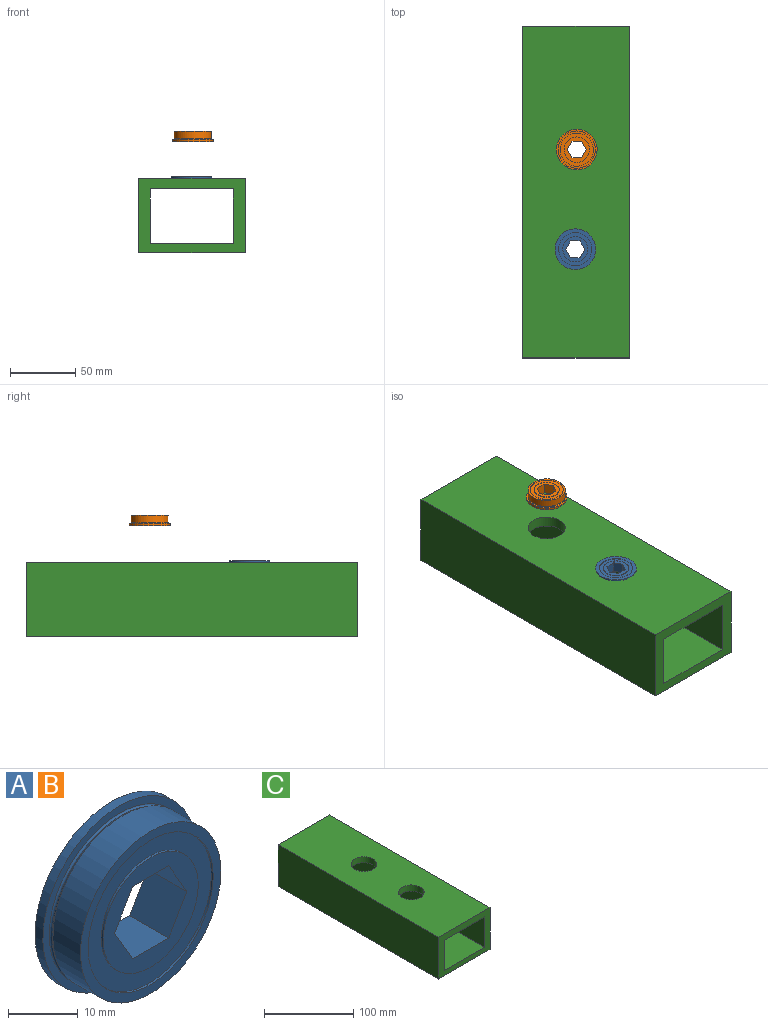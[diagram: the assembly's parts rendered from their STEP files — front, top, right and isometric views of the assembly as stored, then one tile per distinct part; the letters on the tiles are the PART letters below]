
ASSEMBLY  parts=3 mates=2
PART A: 21 faces, bbox 31.1x7.9x31.1 mm
  f0: torus R=14.27mm, axis (0,1,0), area 46.4mm2, adj f4,f10
  f1: cylinder r=9.65mm len=19.3mm, axis (0,1,0), area 23.1mm2, adj f12,f13
  f2: cylinder r=12.7mm len=25.4mm, axis (0,1,0), area 30.4mm2, adj f11,f12
  f3: cylinder r=14.27mm len=28.55mm, axis (0,1,0), area 502.3mm2, adj f4,f11
  f4: cone r=14.06mm half-angle=30deg, axis (0,-1,0), area 38.5mm2, adj f0,f3
  f5: cylinder r=15.56mm len=31.12mm, axis (0,1,0), area 155.2mm2, adj f9,f10
  f6: cylinder r=12.7mm len=25.4mm, axis (0,1,0), area 30.4mm2, adj f8,f9
  f7: cylinder r=9.65mm len=19.3mm, axis (0,1,0), area 23.1mm2, adj f8,f14
  f8: plane 25.4x25.4mm, normal (0,1,0), area 214mm2, adj f6,f7
  f9: plane 31.12x31.12mm, normal (0,1,0), area 253.7mm2, adj f5,f6
  f10: plane 31.12x31.12mm, normal (0,-1,0), area 120.2mm2, adj f0,f5
  f11: plane 28.55x28.55mm, normal (0,-1,0), area 133.5mm2, adj f2,f3
  f12: plane 25.4x25.4mm, normal (0,-1,0), area 214mm2, adj f1,f2
  f13: plane 19.3x19.3mm, normal (0,-1,0), area 152.6mm2, adj f1,f15,f16,f17,f18,f19,f20
  f14: plane 19.3x19.3mm, normal (0,1,0), area 152.6mm2, adj f7,f15,f16,f17,f18,f19,f20
  f15: plane 7.94x6.36mm, normal (-0.87,0,0.5), area 58.3mm2, adj f13,f14,f16,f20
  f16: plane 7.94x6.36mm, normal (-0.87,0,-0.5), area 58.3mm2, adj f13,f14,f15,f17
  f17: plane 7.94x7.34mm, normal (0,0,-1), area 58.3mm2, adj f13,f14,f16,f18
  f18: plane 7.94x6.36mm, normal (0.87,0,-0.5), area 58.3mm2, adj f13,f14,f17,f19
  f19: plane 7.94x6.36mm, normal (0.87,0,0.5), area 58.3mm2, adj f13,f14,f18,f20
  f20: plane 7.94x7.34mm, normal (0,0,1), area 58.3mm2, adj f13,f14,f15,f19
PART B: same geometry as A
PART C: 14 faces, bbox 81.5x254x57.2 mm
  f0: plane 254x81.54mm, normal (0,0,1), area 19428.7mm2, adj f1,f7,f8,f9,f12,f13
  f1: plane 254x57.17mm, normal (-1,0,0), area 14521.1mm2, adj f0,f2,f8,f9
  f2: plane 254x81.54mm, normal (0,0,-1), area 19428.7mm2, adj f1,f7,f8,f9,f10,f11
  f3: plane 254x41.53mm, normal (1,0,0), area 10549.3mm2, adj f4,f6,f8,f9
  f4: plane 254x63.65mm, normal (0,0,-1), area 14884.9mm2, adj f3,f5,f8,f9,f12,f13
  f5: plane 254x41.53mm, normal (-1,0,0), area 10549.3mm2, adj f4,f6,f8,f9
  f6: plane 254x63.65mm, normal (0,0,1), area 14884.9mm2, adj f3,f5,f8,f9,f10,f11
  f7: plane 254x57.17mm, normal (1,0,0), area 14521.1mm2, adj f0,f2,f8,f9
  f8: plane 81.54x57.17mm, normal (0,-1,0), area 2018mm2, adj f0,f1,f2,f3,f4,f5,f6,f7
  f9: plane 81.54x57.17mm, normal (0,1,0), area 2018mm2, adj f0,f1,f2,f3,f4,f5,f6,f7
  f10: cylinder r=14.29mm len=28.58mm, axis (0,0,1), area 659.1mm2, adj f2,f6
  f11: cylinder r=14.29mm len=28.58mm, axis (0,0,1), area 659.1mm2, adj f2,f6
  f12: cylinder r=14.29mm len=28.58mm, axis (0,0,1), area 744.6mm2, adj f0,f4
  f13: cylinder r=14.29mm len=28.58mm, axis (0,0,1), area 744.6mm2, adj f0,f4
PLACE A rot(axis=(1,0,0),90deg) t=(-233.54,-146.48,17.91)mm
PLACE B rot(axis=(-1,0,0),90deg) t=(-232.44,-70.28,60.77)mm
PLACE C t=(-211.18,24.38,6.11)mm
MATE slider B.f0 <-> C.f10  axis (0,0,-1) through (-232.44,-70.28,57.97)mm
MATE cylindrical A.f0 <-> C.f11  axis (0,0,1) through (-233.54,-146.48,20.71)mm
